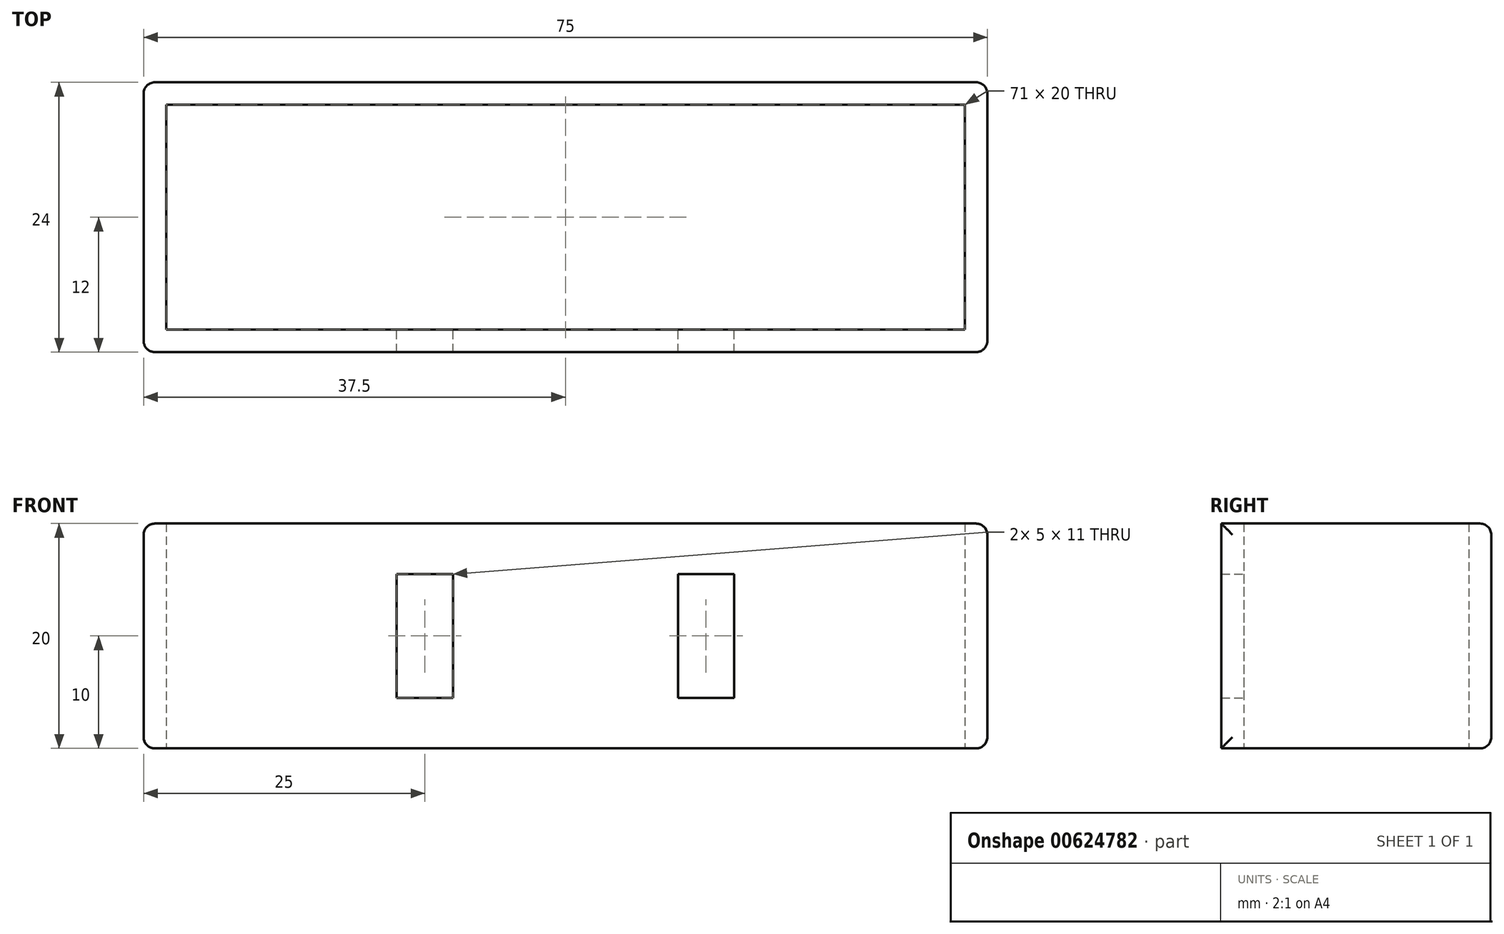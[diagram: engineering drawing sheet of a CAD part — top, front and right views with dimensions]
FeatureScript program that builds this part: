
annotation { "Feature Type Name" : "Feature", "Feature Type Description" : "" }
export const myFeature = defineFeature(function(context is Context, id is Id, definition is map)
    precondition{}
    {
        {
            var Q0;
            Q0=qCreatedBy(makeId("Front.planeOp"),FACE);
            var sketch = newSketch(context, id + "F0", { "sketchPlane" : qUnion([Q0])});
            skLineSegment(sketch, "E0.bottom", {"start": v(0, 0) * mm, "end": v(75, 0) * mm});
            skLineSegment(sketch, "E0.top", {"start": v(0, -20) * mm, "end": v(75, -20) * mm});
            skLineSegment(sketch, "E0.left", {"start": v(0, 0) * mm, "end": v(0, -20) * mm});
            skLineSegment(sketch, "E0.right", {"start": v(75, 0) * mm, "end": v(75, -20) * mm});
            skSolve(sketch);
        }
        {
            var Q0;
            Q0=qSketchRegion(id+"F0",true);
            extrude(context, id + "F1", {"entities" : qUnion([Q0]), "depth" : 24 * mm, "offsetDistance" : 25 * mm});
        }
        {
            var Q0;
            Q0=qCreatedBy(makeId("Top.planeOp"),FACE);
            var sketch = newSketch(context, id + "F2", { "sketchPlane" : qUnion([Q0])});
            skLineSegment(sketch, "E1.bottom", {"start": v(2, -2) * mm, "end": v(73, -2) * mm});
            skLineSegment(sketch, "E1.top", {"start": v(2, -22) * mm, "end": v(73, -22) * mm});
            skLineSegment(sketch, "E1.left", {"start": v(2, -2) * mm, "end": v(2, -22) * mm});
            skLineSegment(sketch, "E1.right", {"start": v(73, -2) * mm, "end": v(73, -22) * mm});
            skSolve(sketch);
        }
        {
            var Q0;
            Q0=qSketchRegion(id+"F2",true);
            extrude(context, id + "F3", {"entities" : qUnion([Q0]), "operationType" : NewBodyOperationType.REMOVE, "endBound" : BoundingType.SYMMETRIC, "depth" : 40 * mm, "offsetDistance" : 25 * mm});
        }
        {
            var Q0;
            Q0=makeQuery(id+"F3.boolean.opBoolean","COPY",FACE,{"derivedFrom":makeQuery(id+"F3.opExtrude","SWEPT_FACE",FACE,{"disambiguationData":[OSD([sQuery(id+"F2.wireOp",EDGE,"E1.top")])]})});
            cPlane(context, id + "F4", {"entities" : qUnion([Q0]), "cplaneType" : CPlaneType.OFFSET, "offset" : 0 * mm, "width" : 150 * mm, "height" : 150 * mm});
        }
        {
            var Q0;
            Q0=qCreatedBy(id+"F4.planeOp",FACE);
            var sketch = newSketch(context, id + "F5", { "sketchPlane" : qUnion([Q0])});
            skLineSegment(sketch, "E2.bottom", {"start": v(-27.5, -4.5) * mm, "end": v(-22.5, -4.5) * mm});
            skLineSegment(sketch, "E3.top", {"start": v(-27.5, -15.5) * mm, "end": v(-22.5, -15.5) * mm});
            skLineSegment(sketch, "E4", {"start": v(-27.5, -4.5) * mm, "end": v(-27.5, -15.5) * mm});
            skLineSegment(sketch, "E5", {"start": v(-22.5, -4.5) * mm, "end": v(-22.5, -15.5) * mm});
            skLineSegment(sketch, "E6", {"start": v(-37.5, 0) * mm, "end": v(-37.5, -20) * mm, "construction": true});
            skLineSegment(sketch, "E7", {"start": v(0, -10) * mm, "end": v(-75, -10) * mm, "construction": true});
            skPoint(sketch, "E8", {"position": v(-37.5, -10) * mm});
            skPoint(sketch, "E9", {"position": v(-20.5, 2.87) * mm});
            skLineSegment(sketch, "E10.bottom", {"start": v(-52.5, -4.5) * mm, "end": v(-47.5, -4.5) * mm});
            skLineSegment(sketch, "E11.top", {"start": v(-52.5, -15.5) * mm, "end": v(-47.5, -15.5) * mm});
            skLineSegment(sketch, "E12", {"start": v(-52.5, -4.5) * mm, "end": v(-52.5, -15.5) * mm});
            skLineSegment(sketch, "E13", {"start": v(-47.5, -4.5) * mm, "end": v(-47.5, -15.5) * mm});
            skSolve(sketch);
        }
        {
            var Q0;
            Q0=qSketchRegion(id+"F5",true);
            extrude(context, id + "F6", {"entities" : qUnion([Q0]), "operationType" : NewBodyOperationType.REMOVE, "oppositeDirection" : true, "depth" : 5 * mm, "offsetDistance" : 25 * mm});
        }
        {
            var Q0;
            Q0=makeQuery(id+"F1.opExtrude","SWEPT_FACE",FACE,{"disambiguationData":[OSD([sQuery(id+"F0.wireOp",EDGE,"E0.right")])]});
            var Q1;
            Q1=makeQuery(id+"F1.opExtrude","CAP_FACE",FACE,{"disambiguationData":[OSD([sQuery(id+"F0.wireOp",EDGE,"E0.bottom"),sQuery(id+"F0.wireOp",EDGE,"E0.top"),sQuery(id+"F0.wireOp",EDGE,"E0.left"),sQuery(id+"F0.wireOp",EDGE,"E0.right")])],"isStart":true});
            var Q2;
            Q2=makeQuery(id+"F1.opExtrude","SWEPT_FACE",FACE,{"disambiguationData":[OSD([sQuery(id+"F0.wireOp",EDGE,"E0.left")])]});
            fillet(context, id + "F7", {"entities" : qUnion([Q0, Q1, Q2]), "radius" : 1 * mm, "tangentPropagation" : true, "allowEdgeOverflow" : false});
        }
    });
